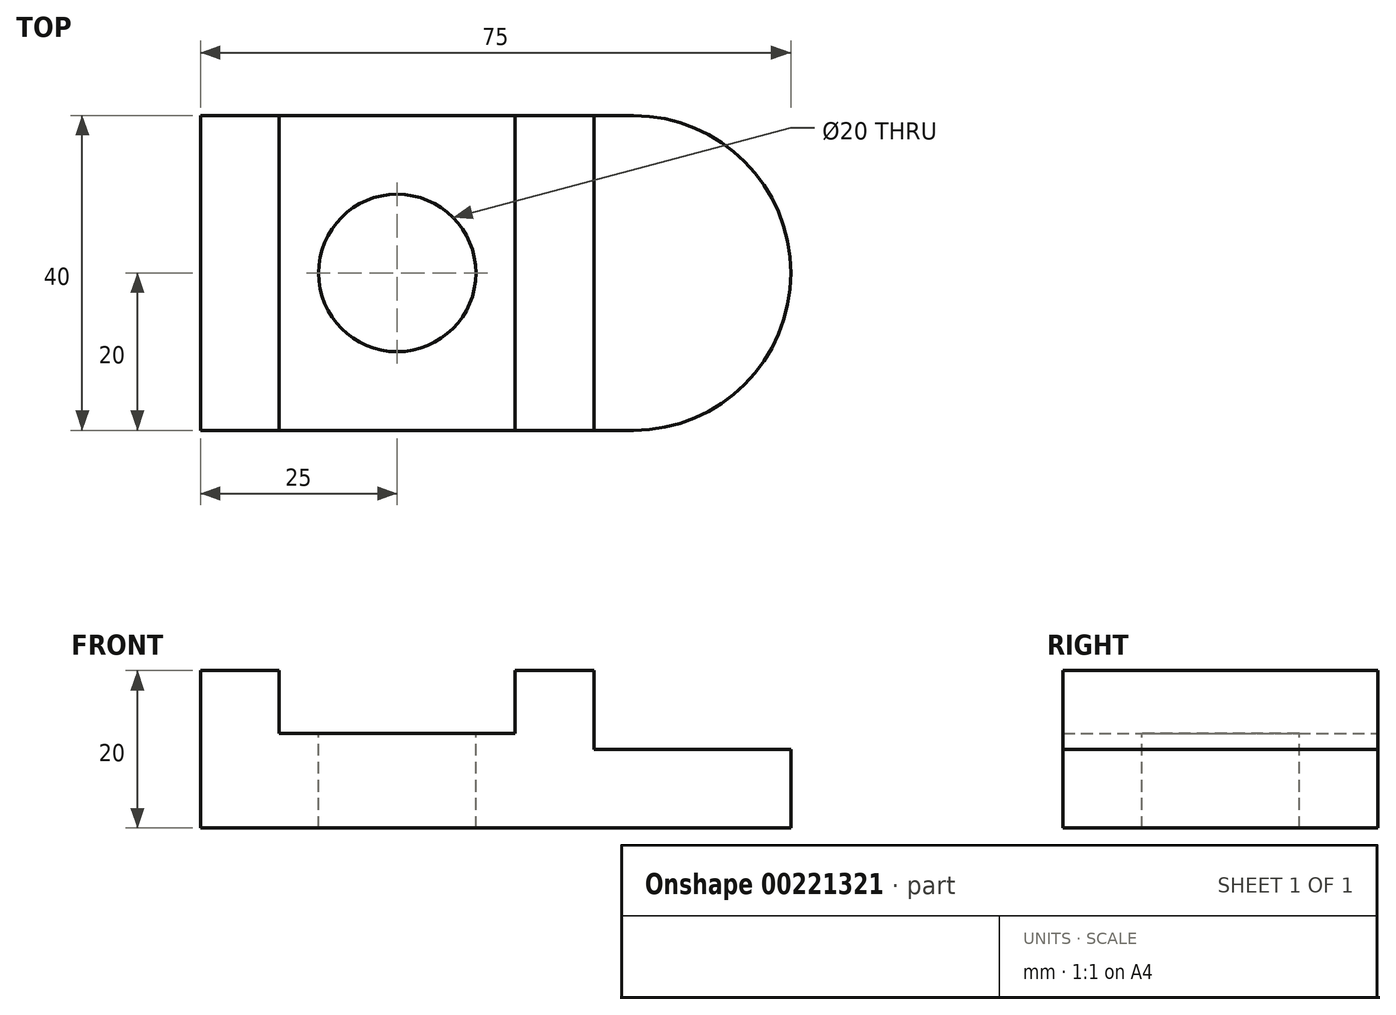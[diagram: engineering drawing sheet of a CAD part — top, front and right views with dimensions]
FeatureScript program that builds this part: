
annotation { "Feature Type Name" : "Feature", "Feature Type Description" : "" }
export const myFeature = defineFeature(function(context is Context, id is Id, definition is map)
    precondition{}
    {
        {
            var Q0;
            Q0=qCreatedBy(makeId("Front.planeOp"),FACE);
            var sketch = newSketch(context, id + "F0", { "sketchPlane" : qUnion([Q0])});
            skLineSegment(sketch, "E0", {"start": v(0, 0) * mm, "end": v(75, 0) * mm});
            skLineSegment(sketch, "E1", {"start": v(75, 0) * mm, "end": v(75, 10) * mm});
            skLineSegment(sketch, "E2", {"start": v(75, 10) * mm, "end": v(50, 10) * mm});
            skLineSegment(sketch, "E3", {"start": v(50, 10) * mm, "end": v(50, 20) * mm});
            skLineSegment(sketch, "E4", {"start": v(50, 20) * mm, "end": v(40, 20) * mm});
            skLineSegment(sketch, "E5", {"start": v(40, 20) * mm, "end": v(40, 12) * mm});
            skLineSegment(sketch, "E6", {"start": v(40, 12) * mm, "end": v(10, 12) * mm});
            skLineSegment(sketch, "E7", {"start": v(10, 12) * mm, "end": v(10, 20) * mm});
            skLineSegment(sketch, "E8", {"start": v(10, 20) * mm, "end": v(0, 20) * mm});
            skLineSegment(sketch, "E9", {"start": v(0, 20) * mm, "end": v(0, 0) * mm});
            skSolve(sketch);
        }
        {
            var Q0;
            Q0=makeQuery(id+"F0.imprint","IMPRINT",FACE,{"disambiguationData":[TD([[makeQuery(id+"F0.imprint","IMPRINT",EDGE,{"derivedFrom":sQuery(id+"F0.wireOp",EDGE,"E0")}),1.0]])]});
            extrude(context, id + "F1", {"entities" : qUnion([Q0]), "depth" : 40 * mm});
        }
        {
            var Q0;
            Q0=makeQuery(id+"F1.opExtrude","CAP_EDGE",EDGE,{"disambiguationData":[OSD([sQuery(id+"F0.wireOp",EDGE,"E1")])],"isStart":false});
            var Q1;
            Q1=makeQuery(id+"F1.opExtrude","CAP_EDGE",EDGE,{"disambiguationData":[OSD([sQuery(id+"F0.wireOp",EDGE,"E1")])],"isStart":true});
            fillet(context, id + "F2", {"entities" : qUnion([Q0, Q1]), "radius" : 20 * mm, "tangentPropagation" : true, "allowEdgeOverflow" : false});
        }
        {
            var Q0;
            Q0=makeQuery(id+"F1.opExtrude","SWEPT_FACE",FACE,{"disambiguationData":[OSD([sQuery(id+"F0.wireOp",EDGE,"E6")])]});
            var sketch = newSketch(context, id + "F3", { "sketchPlane" : qUnion([Q0])});
            skCircle(sketch, "E10", {"center": v(25, -20) * mm, "radius": 10 * mm});
            skSolve(sketch);
        }
        {
            var Q0;
            Q0 = qSketchRegion(id + "F3", true);
            extrude(context, id + "F4", {"entities" : qUnion([Q0]), "operationType" : NewBodyOperationType.REMOVE, "endBound" : BoundingType.THROUGH_ALL, "oppositeDirection" : true, "depth" : 25 * mm});
        }
    });
